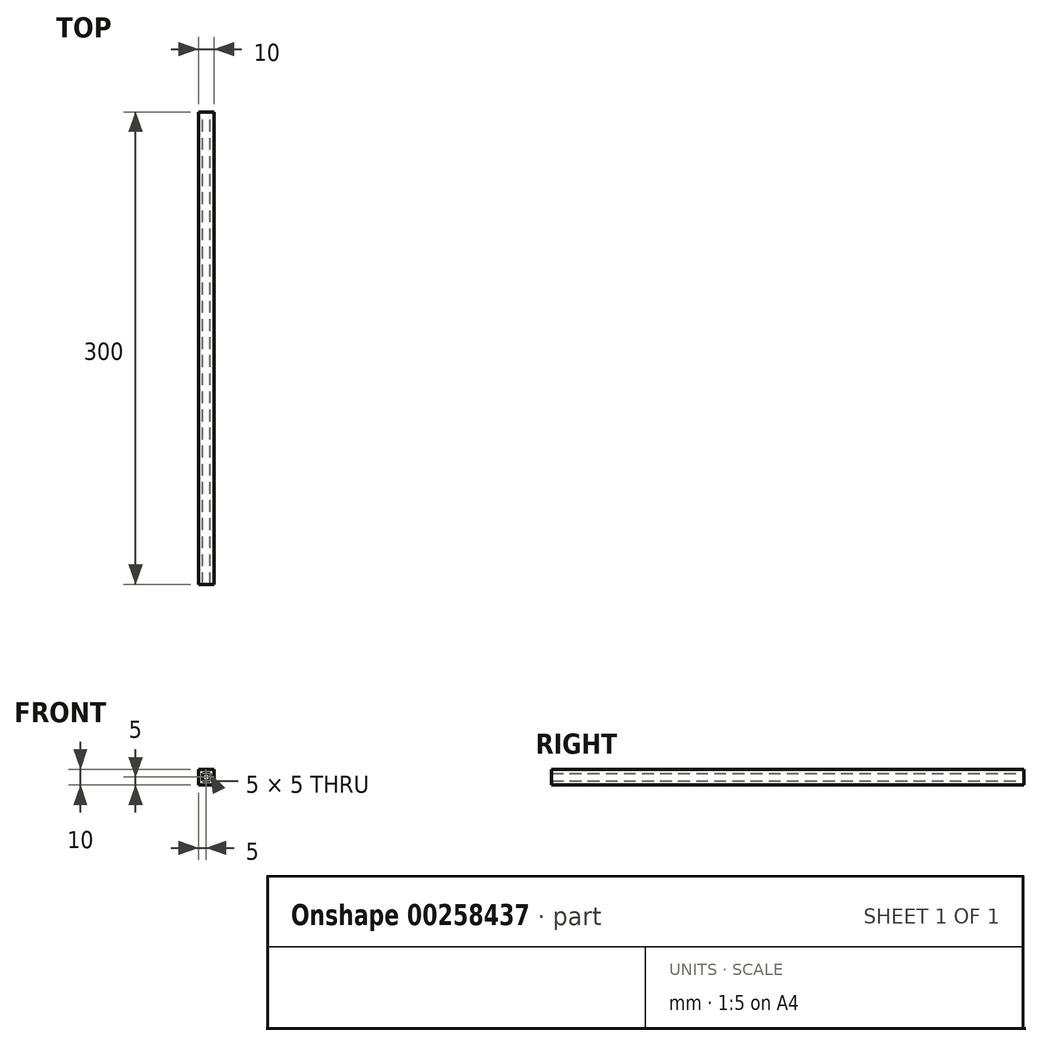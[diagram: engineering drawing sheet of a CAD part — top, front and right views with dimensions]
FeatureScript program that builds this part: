
annotation { "Feature Type Name" : "Feature", "Feature Type Description" : "" }
export const myFeature = defineFeature(function(context is Context, id is Id, definition is map)
    precondition{}
    {
        {
            var Q0;
            Q0=qCreatedBy(makeId("Front.planeOp"),FACE);
            var sketch = newSketch(context, id + "F0", { "sketchPlane" : qUnion([Q0])});
            skLineSegment(sketch, "E0.bottom", {"start": v(5, -5) * mm, "end": v(-5, -5) * mm});
            skLineSegment(sketch, "E0.top", {"start": v(5, 5) * mm, "end": v(-5, 5) * mm});
            skLineSegment(sketch, "E0.left", {"start": v(5, -5) * mm, "end": v(5, 5) * mm});
            skLineSegment(sketch, "E0.right", {"start": v(-5, -5) * mm, "end": v(-5, 5) * mm});
            skPoint(sketch, "E0.middle", {"position": v(0, 0) * mm});
            skLineSegment(sketch, "E1.bottom", {"start": v(2.5, -2.5) * mm, "end": v(-2.5, -2.5) * mm});
            skLineSegment(sketch, "E1.top", {"start": v(2.5, 2.5) * mm, "end": v(-2.5, 2.5) * mm});
            skLineSegment(sketch, "E1.left", {"start": v(2.5, -2.5) * mm, "end": v(2.5, 2.5) * mm});
            skLineSegment(sketch, "E1.right", {"start": v(-2.5, -2.5) * mm, "end": v(-2.5, 2.5) * mm});
            skSolve(sketch);
        }
        {
            var Q0;
            Q0=makeQuery(id+"F0.imprint","IMPRINT",FACE,{"disambiguationData":[TD([[makeQuery(id+"F0.imprint","IMPRINT",EDGE,{"derivedFrom":sQuery(id+"F0.wireOp",EDGE,"E0.bottom")}),-1.0]])]});
            extrude(context, id + "F1", {"entities" : qUnion([Q0]), "depth" : 300 * mm});
        }
    });
